# Revit family: TY-B-TY4151_Imperial
name_source: partatom
category: Sprinklers
units: mm (PartAtom-declared; Revit-internal decimal feet)

## family parameters
Always vertical = Yes
Cut with Voids When Loaded = No
Maintain Annotation Orientation = No
OmniClass Number = 23.65.70.17.11.24
OmniClass Title = Fire Fighting Sprinkler Heads
Part Type = Normal
Room Calculation Point = No
Round Connector Dimension = Use Diameter
Shared = No
Work Plane-Based = No

## types (48) — shared parameters
COBie = Yes
COBie.Component.Name = Sprinklers:Upright_SIN
COBie.Type = Yes
COBie.Type.AssetType = Fixed
COBie.Type.Category = Pr_70_55_97_84:Sprinklers
COBie.Type.DurationUnit = year
COBie.Type.Manufacturer = Tyco Fire Protection Products
COBie.Type.Material = Bronze
COBie.Type.NominalHeight = 0' - 0"
COBie.Type.NominalLength = 0' - 0"
COBie.Type.NominalWidth = 0' - 0"
COBie.Type.Shape = Cylinder
Coverage = Standard
Coverage_ = Standard
Default Elevation = 0' - 0"
K-Factor = 7.9771
Manufacturer = Tyco Fire Protection Products
Manufacturer URL = www.tyco-fire.com
Material_ = Bronze
Model = TY-B
Nominal Diameter 1 = 1"
Orifice = Extra Large
Orifice Size = 1"
Outside Diameter 1 = 1"
Response = Standard
Response_ = Standard
SIN No = TY4151
Takeout 1 = 2"
Technical Data Sheet No = TFP151
zero-valued in all types: COBie.Type.ReplacementCost, Style Id

## per-type parameters (varying)
| type | COBie.Component.Description | COBie.Component.InstallationDate | COBie.Component.WarrantyStartDate | COBie.Type.Colour | COBie.Type.Finish | COBie.Type.ModelNumber | COBie.Type.ModelReference | COBie.Type.Size | COBie.Type.WarrantyGuarantorParts | Description | Finish_ | Part No | Temperature Rating |
| Upright ¾" NPT 135°F Brass_57-590-1-135 | TY-B Wet Upright  135°F K8.0 3/4 NPT Br |  |  | Yellow | Natural Brass | 57-590-1-135 | TY-B Wet Upright  135°F K8.0 3/4 NPT Br | 3/4"(DN20) | http://tycofsbp.com
TFPPTerms_of_Sale.pdf | TY-B Upright Brass 135°F 8K ¾" NPT | Natural Brass | 57-590-1-135 | 135 °F |
| Upright ¾" NPT 155°F Brass_57-590-1-155 | TY-B Wet Upright  155°F K8.0 3/4 NPT Br |  |  | Yellow | Natural Brass | 57-590-1-155 | TY-B Wet Upright  155°F K8.0 3/4 NPT Br | 3/4"(DN20) | http://tycofsbp.com
TFPPTerms_of_Sale.pdf | TY-B Upright Brass 155°F 8K ¾" NPT | Natural Brass | 57-590-1-155 | 155 °F |
| Upright ¾" NPT 175°F Brass_57-590-1-175 | TY-B Wet Upright  175°F K8.0 3/4 NPT Br |  |  | Yellow | Natural Brass | 57-590-1-175 | TY-B Wet Upright  175°F K8.0 3/4 NPT Br | 3/4"(DN20) | http://tycofsbp.com
TFPPTerms_of_Sale.pdf | TY-B Upright Brass 175°F 8K ¾" NPT | Natural Brass | 57-590-1-175 | 175 °F |
| Upright ¾" NPT 200°F Brass_57-590-1-200 | TY-B Wet Upright  200°F K8.0 3/4 NPT Br |  |  | Yellow | Natural Brass | 57-590-1-200 | TY-B Wet Upright  200°F K8.0 3/4 NPT Br | 3/4"(DN20) | http://tycofsbp.com
TFPPTerms_of_Sale.pdf | TY-B Upright Brass 200°F 8K ¾" NPT | Natural Brass | 57-590-1-200 | 200 °F |
| Upright ¾" NPT 286°F Brass_57-590-1-286 | TY-B Wet Upright  286°F K8.0 3/4 NPT Br |  |  | Yellow | Natural Brass | 57-590-1-286 | TY-B Wet Upright  286°F K8.0 3/4 NPT Br | 3/4"(DN20) | http://tycofsbp.com
TFPPTerms_of_Sale.pdf | TY-B Upright Brass 286°F 8K ¾" NPT | Natural Brass | 57-590-1-286 | 286 °F |
| Upright ¾" NPT 360°F Brass_57-590-1-360 | TY-B Wet Upright  360°F K8.0 3/4 NPT Br |  |  | Yellow | Natural Brass | 57-590-1-360 | TY-B Wet Upright  360°F K8.0 3/4 NPT Br | 3/4"(DN20) | http://tycofsbp.com
TFPPTerms_of_Sale.pdf | TY-B Upright Brass 360°F 8K ¾" NPT | Natural Brass | 57-590-1-360 | 360 °F |
| Upright ¾" NPT 135°F White_57-590-2-135 | TY-B Wet Upright  135°F K8.0 3/4 NPT Wh9010 |  |  | Gray | Poly-Stainless Gray | 57-590-2-135 | TY-B Wet Upright  135°F K8.0 3/4 NPT Wh9010 | 3/4"(DN20) | http://tycofsbp.com
TFPPTerms_of_Sale.pdf | TY-B Upright White 135°F 8K ¾" NPT | White RAL9010 | 57-590-2-135 | 135 °F |
| Upright ¾" NPT 135°F White_57-590-2-155 | TY-B Wet Upright_Gray_135  135°F K8.0 3/4 NPT Wh9010 |  |  | Gray | Poly-Stainless Gray | 57-590-2-155 | TY-B Wet Upright_Gray_135  135°F K8.0 3/4 NPT Wh9010 | 3/4"(DN20) | http://tycofsbp.com
TFPPTerms_of_Sale.pdf | TY-B Upright White 135°F 8K ¾" NPT | White RAL9010 | 57-590-2-155 | 135 °F |
| Upright ¾" NPT 135°F White_57-590-2-175 | TY-B Wet Upright_Gray_155  135°F K8.0 3/4 NPT Wh9010 |  |  | Gray | Poly-Stainless Gray | 57-590-2-175 | TY-B Wet Upright_Gray_155  135°F K8.0 3/4 NPT Wh9010 | 3/4"(DN20) | http://tycofsbp.com
TFPPTerms_of_Sale.pdf | TY-B Upright White 135°F 8K ¾" NPT | White RAL9010 | 57-590-2-175 | 135 °F |
| Upright ¾" NPT 135°F White_57-590-2-200 | TY-B Wet Upright_Gray_175  135°F K8.0 3/4 NPT Wh9010 |  |  | Gray | Poly-Stainless Gray | 57-590-2-200 | TY-B Wet Upright_Gray_175  135°F K8.0 3/4 NPT Wh9010 | 3/4"(DN20) | http://tycofsbp.com
TFPPTerms_of_Sale.pdf | TY-B Upright White 135°F 8K ¾" NPT | White RAL9010 | 57-590-2-200 | 135 °F |
| Upright ¾" NPT 135°F White_57-590-2-286 | TY-B Wet Upright_Gray_200  135°F K8.0 3/4 NPT Wh9010 |  |  | Gray | Poly-Stainless Gray | 57-590-2-286 | TY-B Wet Upright_Gray_200  135°F K8.0 3/4 NPT Wh9010 | 3/4"(DN20) | http://tycofsbp.com
TFPPTerms_of_Sale.pdf | TY-B Upright White 135°F 8K ¾" NPT | White RAL9010 | 57-590-2-286 | 135 °F |
| Upright ¾" NPT 135°F White_57-590-2-360 | TY-B Wet Upright_Gray_286  135°F K8.0 3/4 NPT Wh9010 |  |  | Gray | Poly-Stainless Gray | 57-590-2-360 | TY-B Wet Upright_Gray_286  135°F K8.0 3/4 NPT Wh9010 | 3/4"(DN20) | http://tycofsbp.com
TFPPTerms_of_Sale.pdf | TY-B Upright White 135°F 8K ¾" NPT | White RAL9010 | 57-590-2-360 | 135 °F |
| Upright ¾" NPT 135°F White_57-590-3-135 | TY-B Wet Upright  135°F K8.0 3/4 NPT Wh9010 |  |  | White | Pure White | 57-590-3-135 | TY-B Wet Upright  135°F K8.0 3/4 NPT Wh9010 | 3/4"(DN20) | http://tycofsbp.com
TFPPTerms_of_Sale.pdf | TY-B Upright White 135°F 8K ¾" NPT | White RAL9010 | 57-590-3-135 | 135 °F |
| Upright ¾" NPT 155°F White_57-590-3-155 | TY-B Wet Upright  155°F K8.0 3/4 NPT Wh9010 |  |  | White | Pure White | 57-590-3-155 | TY-B Wet Upright  155°F K8.0 3/4 NPT Wh9010 | 3/4"(DN20) | http://tycofsbp.com
TFPPTerms_of_Sale.pdf | TY-B Upright White 155°F 8K ¾" NPT | White RAL9010 | 57-590-3-155 | 155 °F |
| Upright ¾" NPT 175°F  White_57-590-3-175 | TY-B Wet Upright  175°F K8.0 3/4 NPT Wh9010 |  |  | White | Pure White | 57-590-3-175 | TY-B Wet Upright  175°F K8.0 3/4 NPT Wh9010 | 3/4"(DN20) | http://tycofsbp.com
TFPPTerms_of_Sale.pdf | TY-B Upright White 175°F 8K ¾" NPT | White RAL9010 | 57-590-3-175 | 175 °F |
| Upright ¾" NPT 200°F White_57-590-3-200 | TY-B Wet Upright  200°F K8.0 3/4 NPT Wh9010 |  |  | White | Pure White | 57-590-3-200 | TY-B Wet Upright  200°F K8.0 3/4 NPT Wh9010 | 3/4"(DN20) | http://tycofsbp.com
TFPPTerms_of_Sale.pdf | TY-B Upright White 200°F 8K ¾" NPT | White RAL9010 | 57-590-3-200 | 200 °F |
| Upright ¾" NPT 286°F White_57-590-3-286 | TY-B Wet Upright  286°F K8.0 3/4 NPT Wh9010 |  |  | White | Pure White | 57-590-3-286 | TY-B Wet Upright  286°F K8.0 3/4 NPT Wh9010 | 3/4"(DN20) | http://tycofsbp.com
TFPPTerms_of_Sale.pdf | TY-B Upright White 286°F 8K ¾" NPT | White RAL9010 | 57-590-3-286 | 286 °F |
| Upright ¾" NPT 360°F White_57-590-3-360 | TY-B Wet Upright  360°F K8.0 3/4 NPT Wh9010 |  |  | White | Pure White | 57-590-3-360 | TY-B Wet Upright  360°F K8.0 3/4 NPT Wh9010 | 3/4"(DN20) | http://tycofsbp.com
TFPPTerms_of_Sale.pdf | TY-B Upright White 360°F 8K ¾" NPT | White RAL9010 | 57-590-3-360 | 360 °F |
| Upright ¾" NPT 135°F White_57-590-4-135 | TY-B Wet Upright  57.2°C K115 DN20 NPT Wh9003 |  |  | White | Signal White | 57-590-4-135 | TY-B Wet Upright  57.2°C K115 DN20 NPT Wh9003 | 3/4"(DN20) | http://tycofsbp.com | TY-B Upright White 135°F 8K ¾" NPT | White RAL9003 | 57-590-4-135 | 135 °F |
| Upright ¾" NPT 155°F White_57-590-4-155 | TY-B Wet Upright  68.3°C K115 DN20 NPT Wh9003 |  |  | White | Signal White | 57-590-4-155 | TY-B Wet Upright  68.3°C K115 DN20 NPT Wh9003 | 3/4"(DN20) | http://tycofsbp.com | TY-B Upright White 155°F 8K ¾" NPT | White RAL9003 | 57-590-4-155 | 155 °F |
| Upright ¾" NPT 175°F White_57-590-4-175 | TY-B Wet Upright  79.4°C K115 DN20 NPT Wh9003 |  |  | White | Signal White | 57-590-4-175 | TY-B Wet Upright  79.4°C K115 DN20 NPT Wh9003 | 3/4"(DN20) | http://tycofsbp.com | TY-B Upright White 175°F 8K ¾" NPT | White RAL9003 | 57-590-4-175 | 175 °F |
| Upright ¾" NPT 200°F White_57-590-4-200 | TY-B Wet Upright  93.3°C K115 DN20 NPT Wh9003 |  |  | White | Signal White | 57-590-4-200 | TY-B Wet Upright  93.3°C K115 DN20 NPT Wh9003 | 3/4"(DN20) | http://tycofsbp.com | TY-B Upright White 200°F 8K ¾" NPT | White RAL9003 | 57-590-4-200 | 200 °F |
| Upright ¾" NPT 286°F White_57-590-4-286 | TY-B Wet Upright  141.1°C K115 DN20 NPT Wh9003 | 1900-12-31T23:59:59 | 1900-12-31T23:59:59 | White |  | 57-590-4-286 | TY-B Wet Upright  141.1°C K115 DN20 NPT Wh9003 | 3/4"(DN20) | http://tycofsbp.com | TY-B Upright White 286°F 8K ¾" NPT | White RAL9003 | 57-590-4-286 | 286 °F |
| Upright ¾" NPT 360°F White_57-590-4-360 | TY-B Wet Upright  182.2°C K115 DN20 NPT Wh9003 |  |  | White | Signal White | 57-590-4-360 | TY-B Wet Upright  182.2°C K115 DN20 NPT Wh9003 | 3/4"(DN20) | http://tycofsbp.com | TY-B Upright White 360°F 8K ¾" NPT | White RAL9003 | 57-590-4-360 | 360 °F |
| Upright ¾" NPT 155°F JetBlack_57-590-5-155 | TY-B Wet Upright  68.3°C K115 DN20 NPT JBlk |  |  | Black | Jet Black | 57-590-5-155 | TY-B Wet Upright  68.3°C K115 DN20 NPT JBlk | 3/4"(DN20) | http://tycofsbp.com | TY-B Upright JetBlack 155°F 8K ¾" NPT | Jet Black RAL9005 | 57-590-5-155 | 155 °F |
| Upright ¾" NPT 200°F JetBlack_57-590-5-200 | TY-B Wet Upright  93.3°C K115 DN20 NPT JBlk |  |  | Black | Jet Black | 57-590-5-200 | TY-B Wet Upright  93.3°C K115 DN20 NPT JBlk | 3/4"(DN20) | http://tycofsbp.com | TY-B Upright JetBlack 200°F 8K ¾" NPT | Jet Black RAL9005 | 57-590-5-200 | 200 °F |
| Upright ¾" NPT 135°F Wax_57-590-6-135 | TY-B Wet Upright  135°F K8.0 3/4 NPT Wx |  |  | Gray | Wax Coated | 57-590-6-135 | TY-B Wet Upright  135°F K8.0 3/4 NPT Wx | 3/4"(DN20) | http://tycofsbp.com
TFPPTerms_of_Sale.pdf | TY-B Upright Wax 135°F 8K ¾" NPT | Wax Coated | 57-590-6-135 | 135 °F |
| Upright ¾" NPT 155°F Wax_57-590-6-155 | TY-B Wet Upright  155°F K8.0 3/4 NPT Wx |  |  | Gray | Wax Coated | 57-590-6-155 | TY-B Wet Upright  155°F K8.0 3/4 NPT Wx | 3/4"(DN20) | http://tycofsbp.com
TFPPTerms_of_Sale.pdf | TY-B Upright Wax 155°F 8K ¾" NPT | Wax Coated | 57-590-6-155 | 155 °F |
| Upright ¾" NPT 175°F Wax_57-590-6-175 | TY-B Wet Upright  175°F K8.0 3/4 NPT Wx |  |  | Gray | Wax Coated | 57-590-6-175 | TY-B Wet Upright  175°F K8.0 3/4 NPT Wx | 3/4"(DN20) | http://tycofsbp.com
TFPPTerms_of_Sale.pdf | TY-B Upright Wax 175°F 8K ¾" NPT | Wax Coated | 57-590-6-175 | 175 °F |
| Upright ¾" NPT 200°F Wax_57-590-6-200 | TY-B Wet Upright  200°F K8.0 3/4 NPT Wx |  |  | Gray | Wax Coated | 57-590-6-200 | TY-B Wet Upright  200°F K8.0 3/4 NPT Wx | 3/4"(DN20) | http://tycofsbp.com
TFPPTerms_of_Sale.pdf | TY-B Upright Wax 200°F 8K ¾" NPT | Wax Coated | 57-590-6-200 | 200 °F |
| Upright ¾" NPT 286°F Wax_57-590-6-286 | TY-B Wet Upright  286°F K8.0 3/4 NPT Wx |  |  | Gray | Wax Coated | 57-590-6-286 | TY-B Wet Upright  286°F K8.0 3/4 NPT Wx | 3/4"(Dn20) | http://tycofsbp.com
TFPPTerms_of_Sale.pdf | TY-B Upright Wax 286°F 8K ¾" NPT | Wax Coated | 57-590-6-286 | 286 °F |
| Upright ¾" NPT 135°F Lead_57-590-7-135 | TY-B Wet Upright  135°F K8.0 3/4 NPT Lead |  |  | Gray | Lead Coated | 57-590-7-135 | TY-B Wet Upright  135°F K8.0 3/4 NPT Lead | 3/4"(DN20) | http://tycofsbp.com
TFPPTerms_of_Sale.pdf | TY-B Upright Lead 135°F 8K ¾" NPT | Lead Coated | 57-590-7-135 | 135 °F |
| Upright ¾" NPT 155°F Lead_57-590-7-155 | TY-B Wet Upright  155°F K8.0 3/4 NPT Lead |  |  | Gray | Lead Coated | 57-590-7-155 | TY-B Wet Upright  155°F K8.0 3/4 NPT Lead | 3/4"(DN20) | http://tycofsbp.com
TFPPTerms_of_Sale.pdf | TY-B Upright Lead 155°F 8K ¾" NPT | Lead Coated | 57-590-7-155 | 155 °F |
| Upright ¾" NPT 175°F Lead_57-590-7-175 | TY-B Wet Upright  175°F K8.0 3/4 NPT Lead |  |  | Gray | Lead Coated | 57-590-7-175 | TY-B Wet Upright  175°F K8.0 3/4 NPT Lead | 3/4"(DN20) | http://tycofsbp.com
TFPPTerms_of_Sale.pdf | TY-B Upright Lead 175°F 8K ¾" NPT | Lead Coated | 57-590-7-175 | 175 °F |
| Upright ¾" NPT 200°F Lead_57-590-7-200 | TY-B Wet Upright  200°F K8.0 3/4 NPT Lead |  |  | Gray | Lead Coated | 57-590-7-200 | TY-B Wet Upright  200°F K8.0 3/4 NPT Lead | 3/4"(DN20) | http://tycofsbp.com
TFPPTerms_of_Sale.pdf | TY-B Upright Lead 200°F 8K ¾" NPT | Lead Coated | 57-590-7-200 | 200 °F |
| Upright ¾" NPT 286°F Lead_57-590-7-286 | TY-B Wet Upright  286°F K8.0 3/4 NPT Lead |  |  | Gray | Lead Coated | 57-590-7-286 | TY-B Wet Upright  286°F K8.0 3/4 NPT Lead | 3/4"(DN20) | http://tycofsbp.com
TFPPTerms_of_Sale.pdf | TY-B Upright Lead 286°F 8K ¾" NPT | Lead Coated | 57-590-7-286 | 286 °F |
| Upright ¾" NPT 360°F Lead_57-590-7-360 | TY-B Wet Upright  360°F K8.0 3/4 NPT Lead |  |  | Gray | Lead Coated | 57-590-7-360 | TY-B Wet Upright  360°F K8.0 3/4 NPT Lead | 3/4"(DN20) | http://tycofsbp.com
TFPPTerms_of_Sale.pdf | TY-B Upright Lead 360°F 8K ¾" NPT | Lead Coated | 57-590-7-360 | 360 °F |
| Upright ¾" NPT 135°F Wax Over Lead_57-590-8-135 | TY-B Wet Upright  135°F K8.0 3/4 NPT WoL |  |  | Gray | Wax-Over Lead | 57-590-8-135 | TY-B Wet Upright  135°F K8.0 3/4 NPT WoL | 3/4"(DN20) | http://tycofsbp.com
TFPPTerms_of_Sale.pdf | TY-B Upright Wax Over Lead 135°F 8K ¾" NPT | Wax Over Lead | 57-590-8-135 | 135 °F |
| Upright ¾" NPT 155°F Wax Over Lead_57-590-8-155 | TY-B Wet Upright  155°F K8.0 3/4 NPT WoL |  |  | Gray | Wax-Over-Lead | 57-590-8-155 | TY-B Wet Upright  155°F K8.0 3/4 NPT WoL | 3/4"(DN20) | http://tycofsbp.com
TFPPTerms_of_Sale.pdf | TY-B Upright Wax Over Lead 155°F 8K ¾" NPT | Wax Over Lead | 57-590-8-155 | 155 °F |
| Upright ¾" NPT 175°F Wax Over Lead_57-590-8-175 | TY-B Wet Upright  175°F K8.0 3/4 NPT WoL |  |  | Gray | Wax-Over-Lead | 57-590-8-175 | TY-B Wet Upright  175°F K8.0 3/4 NPT WoL | 3/4"(DN20) | http://tycofsbp.com
TFPPTerms_of_Sale.pdf | TY-B Upright Wax Over Lead 175°F 8K ¾" NPT | Wax Over Lead | 57-590-8-175 | 175 °F |
| Upright ¾" NPT 200°F Wax Over Lead_57-590-8-200 | TY-B Wet Upright  200°F K8.0 3/4 NPT WoL |  |  | Gray | Wax-Over-Lead | 57-590-8-200 | TY-B Wet Upright  200°F K8.0 3/4 NPT WoL | 3/4"(DN20) | http://tycofsbp.com
TFPPTerms_of_Sale.pdf | TY-B Upright Wax Over Lead 200°F 8K ¾" NPT | Wax Over Lead | 57-590-8-200 | 200 °F |
| Upright ¾" NPT 286°F Wax Over Lead_57-590-8-286 | TY-B Wet Upright  286°F K8.0 3/4 NPT WoL |  |  | Gray | Wax-Over-Lead | 57-590-8-286 | TY-B Wet Upright  286°F K8.0 3/4 NPT WoL | 3/4"(DN20) | http://tycofsbp.com
TFPPTerms_of_Sale.pdf | TY-B Upright Wax Over Lead 286°F 8K ¾" NPT | Wax Over Lead | 57-590-8-286 | 286 °F |
| Upright ¾" NPT 135°F Chrome_57-590-9-135 | TY-B Wet Upright  135°F K8.0 3/4 NPT Chr |  |  | Silver | Chrome Plated | 57-590-9-135 | TY-B Wet Upright  135°F K8.0 3/4 NPT Chr | 3/4"(DN20) | http://tycofsbp.com
TFPPTerms_of_Sale.pdf | TY-B Upright Chrome 135°F 8K ¾" NPT | Chrome Plated | 57-590-9-135 | 135 °F |
| Upright ¾" NPT 155°F Chrome_57-590-9-155 | TY-B Wet Upright  155°F K8.0 3/4 NPT Chr |  |  | Silver | Chrome Plated | 57-590-9-155 | TY-B Wet Upright  155°F K8.0 3/4 NPT Chr | 3/4"(DN20) | http://tycofsbp.com
TFPPTerms_of_Sale.pdf | TY-B Upright Chrome 155°F 8K ¾" NPT | Chrome Plated | 57-590-9-155 | 155 °F |
| Upright ¾" NPT 175°F Chrome_57-590-9-175 | TY-B Wet Upright  175°F K8.0 3/4 NPT Chr |  |  | Silver | Chrome Plated | 57-590-9-175 | TY-B Wet Upright  175°F K8.0 3/4 NPT Chr | 3/4"(DN20) | http://tycofsbp.com
TFPPTerms_of_Sale.pdf | TY-B Upright Chrome 175°F 8K ¾" NPT | Chrome Plated | 57-590-9-175 | 175 °F |
| Upright ¾" NPT 200°F Chrome_57-590-9-200 | TY-B Wet Upright  200°F K8.0 3/4 NPT Chr |  |  | Silver | Chrome Plated | 57-590-9-200 | TY-B Wet Upright  200°F K8.0 3/4 NPT Chr | 3/4"(DN20) | http://tycofsbp.com
TFPPTerms_of_Sale.pdf | TY-B Upright Chrome 200°F 8K ¾" NPT | Chrome Plated | 57-590-9-200 | 200 °F |
| Upright ¾" NPT 286°F Chrome_57-590-9-286 | TY-B Wet Upright  286°F K8.0 3/4 NPT Chr |  |  | Silver | Chrome Plated | 57-590-9-286 | TY-B Wet Upright  286°F K8.0 3/4 NPT Chr | 3/4"(DN20) | http://tycofsbp.com
TFPPTerms_of_Sale.pdf | TY-B Upright Chrome 286°F 8K ¾" NPT | Chrome Plated | 57-590-9-286 | 286 °F |
| Upright ¾" NPT 360°F Chrome_57-590-9-360 | TY-B Wet Upright  360°F K8.0 3/4 NPT Chr |  |  | Silver | Chrome plated | 57-590-9-360 | TY-B Wet Upright  360°F K8.0 3/4 NPT Chr | 3/4"(DN20) | http://tycofsbp.com
TFPPTerms_of_Sale.pdf | TY-B Upright Chrome 360°F 8K ¾" NPT | Chrome Plated | 57-590-9-360 | 360 °F |

## geometry (parser evidence)
native form markers: Blend x2, Sweep x63
no freeform markers — native parametric forms only
